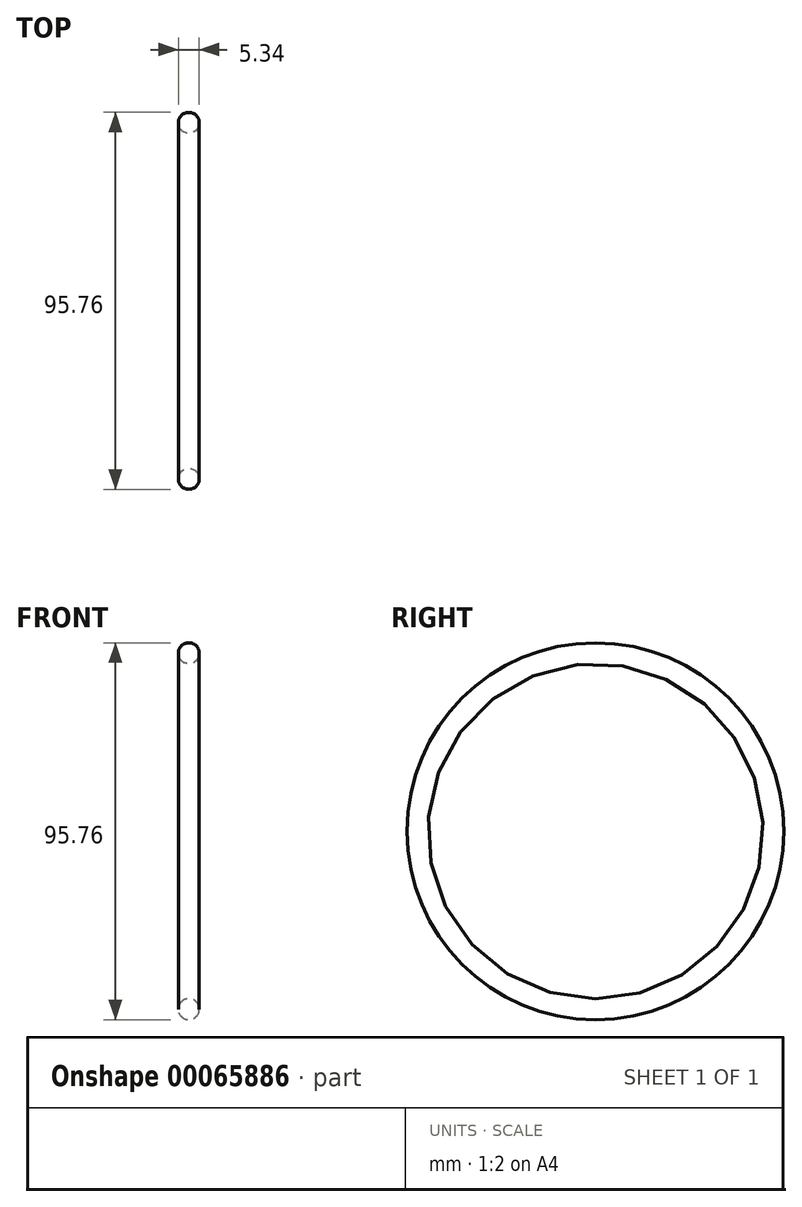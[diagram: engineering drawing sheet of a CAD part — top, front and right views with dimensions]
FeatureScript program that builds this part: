
annotation { "Feature Type Name" : "Feature", "Feature Type Description" : "" }
export const myFeature = defineFeature(function(context is Context, id is Id, definition is map)
    precondition{}
    {
        {
            var Q0;
            Q0=qCreatedBy(makeId("Front.planeOp"),FACE);
            var sketch = newSketch(context, id + "F0", { "sketchPlane" : qUnion([Q0])});
            skLineSegment(sketch, "E0", {"start": v(0, 0) * mm, "end": v(-6.06, 0) * mm, "construction": true});
            skCircle(sketch, "E1", {"center": v(0, 45.21) * mm, "radius": 2.67 * mm});
            skSolve(sketch);
        }
        {
            var Q0;
            Q0=makeQuery(id+"F0.imprint","IMPRINT",FACE,{"disambiguationData":[TD([[makeQuery(id+"F0.imprint","IMPRINT",EDGE,{"derivedFrom":sQuery(id+"F0.wireOp",EDGE,"E1")}),1.0]])]});
            var Q1;
            Q1=sQuery(id+"F0.wireOp",EDGE,"E0");
            revolve(context, id + "F1", {"entities" : qUnion([Q0]), "axis" : qUnion([Q1]), "revolveType" : RevolveType.FULL});
        }
    });
